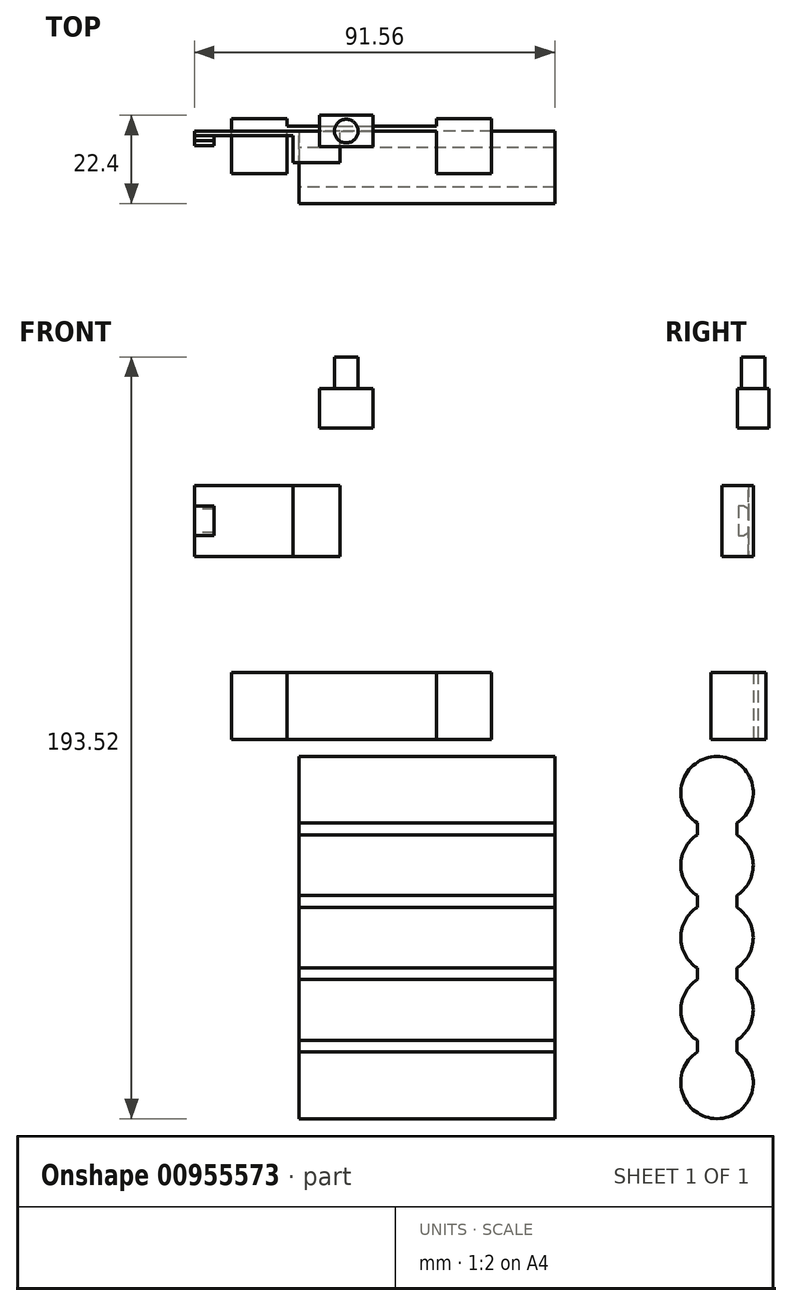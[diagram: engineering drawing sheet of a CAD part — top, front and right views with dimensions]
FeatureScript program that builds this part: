
annotation { "Feature Type Name" : "Feature", "Feature Type Description" : "" }
export const myFeature = defineFeature(function(context is Context, id is Id, definition is map)
    precondition{}
    {
        {
            var Q0;
            Q0=qCreatedBy(makeId("Front.planeOp"),FACE);
            var sketch = newSketch(context, id + "F0", { "sketchPlane" : qUnion([Q0])});
            skLineSegment(sketch, "E0.bottom", {"start": v(-22.06, 31.07) * mm, "end": v(-59.06, 31.07) * mm});
            skLineSegment(sketch, "E0.top", {"start": v(-22.06, 13.07) * mm, "end": v(-59.06, 13.07) * mm});
            skLineSegment(sketch, "E0.left", {"start": v(-22.06, 31.07) * mm, "end": v(-22.06, 13.07) * mm});
            skLineSegment(sketch, "E0.right", {"start": v(-59.06, 31.07) * mm, "end": v(-59.06, 13.07) * mm});
            skLineSegment(sketch, "E1.bottom", {"start": v(-49.58, -16.42) * mm, "end": v(16.42, -16.42) * mm});
            skLineSegment(sketch, "E1.top", {"start": v(-49.58, -33.42) * mm, "end": v(16.42, -33.42) * mm});
            skLineSegment(sketch, "E1.left", {"start": v(-49.58, -16.42) * mm, "end": v(-49.58, -33.42) * mm});
            skLineSegment(sketch, "E1.right", {"start": v(16.42, -16.42) * mm, "end": v(16.42, -33.42) * mm});
            skLineSegment(sketch, "E2.bottom", {"start": v(-27.25, 55.7) * mm, "end": v(-13.75, 55.7) * mm});
            skLineSegment(sketch, "E2.top", {"start": v(-27.25, 45.7) * mm, "end": v(-13.75, 45.7) * mm});
            skLineSegment(sketch, "E2.left", {"start": v(-27.25, 55.7) * mm, "end": v(-27.25, 45.7) * mm});
            skLineSegment(sketch, "E2.right", {"start": v(-13.75, 55.7) * mm, "end": v(-13.75, 45.7) * mm});
            skLineSegment(sketch, "E3", {"start": v(-20.5, 55.7) * mm, "end": v(-20.5, 63.7) * mm});
            skPoint(sketch, "E3.endSnap0", {"position": v(-20.5, 55.7) * mm});
            skLineSegment(sketch, "E4", {"start": v(-20.5, 63.7) * mm, "end": v(-17.5, 63.7) * mm});
            skLineSegment(sketch, "E5", {"start": v(-17.5, 63.7) * mm, "end": v(-17.5, 55.7) * mm});
            skLineSegment(sketch, "E6", {"start": v(-35.58, -16.42) * mm, "end": v(-35.58, -33.42) * mm});
            skLineSegment(sketch, "E7", {"start": v(2.42, -16.42) * mm, "end": v(2.42, -33.42) * mm});
            skSolve(sketch);
        }
        {
            var Q0;
            Q0=qCreatedBy(makeId("Right.planeOp"),FACE);
            var sketch = newSketch(context, id + "F1", { "sketchPlane" : qUnion([Q0])});
            skLineSegment(sketch, "E8.bottom", {"start": v(0, -47.02) * mm, "end": v(-18.4, -47.02) * mm});
            skLineSegment(sketch, "E8.top", {"start": v(0, -120.62) * mm, "end": v(-18.4, -120.62) * mm});
            skLineSegment(sketch, "E8.left", {"start": v(0, -47.02) * mm, "end": v(0, -120.62) * mm, "construction": true});
            skLineSegment(sketch, "E8.right", {"start": v(-18.4, -47.02) * mm, "end": v(-18.4, -120.62) * mm, "construction": true});
            skCircle(sketch, "E9", {"center": v(-9.2, -47.02) * mm, "radius": 9.2 * mm});
            skCircle(sketch, "E10", {"center": v(-9.2, -65.42) * mm, "radius": 9.2 * mm});
            skCircle(sketch, "E11", {"center": v(-9.2, -83.82) * mm, "radius": 9.2 * mm});
            skCircle(sketch, "E12", {"center": v(-9.2, -120.62) * mm, "radius": 9.2 * mm});
            skLineSegment(sketch, "E13", {"start": v(-14.2, -54.74) * mm, "end": v(-14.2, -112.9) * mm});
            skLineSegment(sketch, "E14", {"start": v(-4.2, -54.74) * mm, "end": v(-4.2, -112.9) * mm});
            skCircle(sketch, "E15", {"center": v(-9.2, -102.22) * mm, "radius": 9.2 * mm});
            skSolve(sketch);
        }
        {
            var Q0;
            Q0 = qSketchRegion(id + "F1", true);
            extrude(context, id + "F2", {"entities" : qUnion([Q0]), "endBound" : BoundingType.SYMMETRIC, "depth" : 65 * mm, "offsetDistance" : 25 * mm});
        }
        {
            var Q0;
            {var subQ0=sQuery(id+"F0.wireOp",EDGE,"E6");Q0=makeQuery(id+"F0.imprint","IMPRINT",FACE,{"disambiguationData":[TD([[makeQuery(id+"F0.imprint","IMPRINT",EDGE,{"derivedFrom":subQ0}),1.0]])]});}
            extrude(context, id + "F3", {"entities" : qUnion([Q0]), "oppositeDirection" : true, "depth" : 1.2 * mm, "offsetDistance" : 25 * mm});
        }
        {
            var Q0;
            Q0=makeQuery(id+"F0.imprint","IMPRINT",FACE,{"disambiguationData":[TD([[makeQuery(id+"F0.imprint","IMPRINT",EDGE,{"derivedFrom":sQuery(id+"F0.wireOp",EDGE,"E0.bottom")}),1.0]])]});
            extrude(context, id + "F4", {"entities" : qUnion([Q0]), "depth" : 1.2 * mm, "offsetDistance" : 25 * mm});
        }
        {
            var Q0;
            Q0=makeQuery(id+"F0.imprint","IMPRINT",FACE,{"disambiguationData":[TD([[makeQuery(id+"F0.imprint","IMPRINT",EDGE,{"derivedFrom":sQuery(id+"F0.wireOp",EDGE,"E2.top")}),1.0]])]});
            extrude(context, id + "F5", {"entities" : qUnion([Q0]), "endBound" : BoundingType.SYMMETRIC, "depth" : 8 * mm, "offsetDistance" : 25 * mm});
        }
        {
            var Q0;
            {var subQ0=sQuery(id+"F0.wireOp",EDGE,"E3");Q0=makeQuery(id+"F0.imprint","IMPRINT",FACE,{"disambiguationData":[TD([[makeQuery(id+"F0.imprint","IMPRINT",EDGE,{"derivedFrom":subQ0}),-1.0]])]});}
            var Q1;
            Q1=sQuery(id+"F0.wireOp",EDGE,"E3");
            revolve(context, id + "F6", {"operationType" : NewBodyOperationType.ADD, "surfaceOperationType" : NewSurfaceOperationType.NEW, "entities" : qUnion([Q0]), "axis" : qUnion([Q1]), "revolveType" : RevolveType.FULL});
        }
        {
            var Q0;
            {var subQ0=sQuery(id+"F0.wireOp",EDGE,"E1.left");Q0=makeQuery(id+"F0.imprint","IMPRINT",FACE,{"disambiguationData":[TD([[makeQuery(id+"F0.imprint","IMPRINT",EDGE,{"derivedFrom":subQ0}),1.0]])]});}
            var Q1;
            {var subQ0=sQuery(id+"F0.wireOp",EDGE,"E1.right");Q1=makeQuery(id+"F0.imprint","IMPRINT",FACE,{"disambiguationData":[TD([[makeQuery(id+"F0.imprint","IMPRINT",EDGE,{"derivedFrom":subQ0}),-1.0]])]});}
            extrude(context, id + "F7", {"entities" : qUnion([Q0, Q1]), "operationType" : NewBodyOperationType.ADD, "depth" : (14 - 3.2) * mm, "offsetDistance" : 25 * mm, "hasSecondDirection" : true, "secondDirectionOppositeDirection" : true, "secondDirectionDepth" : 3.2 * mm});
        }
        {
            var Q0;
            Q0=makeQuery(id+"F4.opExtrude","SWEPT_FACE",FACE,{"disambiguationData":[OSD([sQuery(id+"F0.wireOp",EDGE,"E0.right")])]});
            var sketch = newSketch(context, id + "F8", { "sketchPlane" : qUnion([Q0])});
            skLineSegment(sketch, "E16", {"start": v(1.2, 25.1) * mm, "end": v(2.45, 25.82) * mm});
            skLineSegment(sketch, "E17", {"start": v(2.45, 25.82) * mm, "end": v(3.7, 25.82) * mm});
            skLineSegment(sketch, "E18", {"start": v(3.7, 25.82) * mm, "end": v(3.7, 18.32) * mm});
            skLineSegment(sketch, "E19", {"start": v(3.7, 18.32) * mm, "end": v(2.45, 18.32) * mm});
            skLineSegment(sketch, "E20", {"start": v(2.45, 18.32) * mm, "end": v(1.2, 19.04) * mm});
            skPoint(sketch, "E21", {"position": v(3.7, 22.07) * mm});
            skPoint(sketch, "E22", {"position": v(1.2, 22.07) * mm});
            skSolve(sketch);
        }
        {
            var Q0;
            {var subQ0=sQuery(id+"F8.wireOp",EDGE,"E16");Q0=makeQuery(id+"F8.imprint","IMPRINT",FACE,{"disambiguationData":[TD([[makeQuery(id+"F8.imprint","IMPRINT",EDGE,{"derivedFrom":subQ0}),-1.0]])]});}
            extrude(context, id + "F9", {"entities" : qUnion([Q0]), "operationType" : NewBodyOperationType.ADD, "oppositeDirection" : true, "depth" : 5 * mm, "offsetDistance" : 25 * mm});
        }
        {
            var Q0;
            Q0=makeQuery(id+"F4.opExtrude","CAP_FACE",FACE,{"disambiguationData":[OSD([sQuery(id+"F0.wireOp",EDGE,"E0.bottom"),sQuery(id+"F0.wireOp",EDGE,"E0.top"),sQuery(id+"F0.wireOp",EDGE,"E0.left"),sQuery(id+"F0.wireOp",EDGE,"E0.right")])],"isStart":true});
            var sketch = newSketch(context, id + "F10", { "sketchPlane" : qUnion([Q0])});
            skLineSegment(sketch, "E23", {"start": v(34.06, 31.07) * mm, "end": v(34.06, 13.07) * mm});
            skSolve(sketch);
        }
        {
            var Q0;
            {var subQ0=sQuery(id+"F10.wireOp",EDGE,"E23");Q0=makeQuery(id+"F10.imprint","IMPRINT",FACE,{"disambiguationData":[TD([[makeQuery(id+"F10.imprint","IMPRINT",EDGE,{"derivedFrom":subQ0}),-1.0]])]});}
            extrude(context, id + "F11", {"entities" : qUnion([Q0]), "operationType" : NewBodyOperationType.ADD, "oppositeDirection" : true, "depth" : 8 * mm, "offsetDistance" : 25 * mm});
        }
    });
